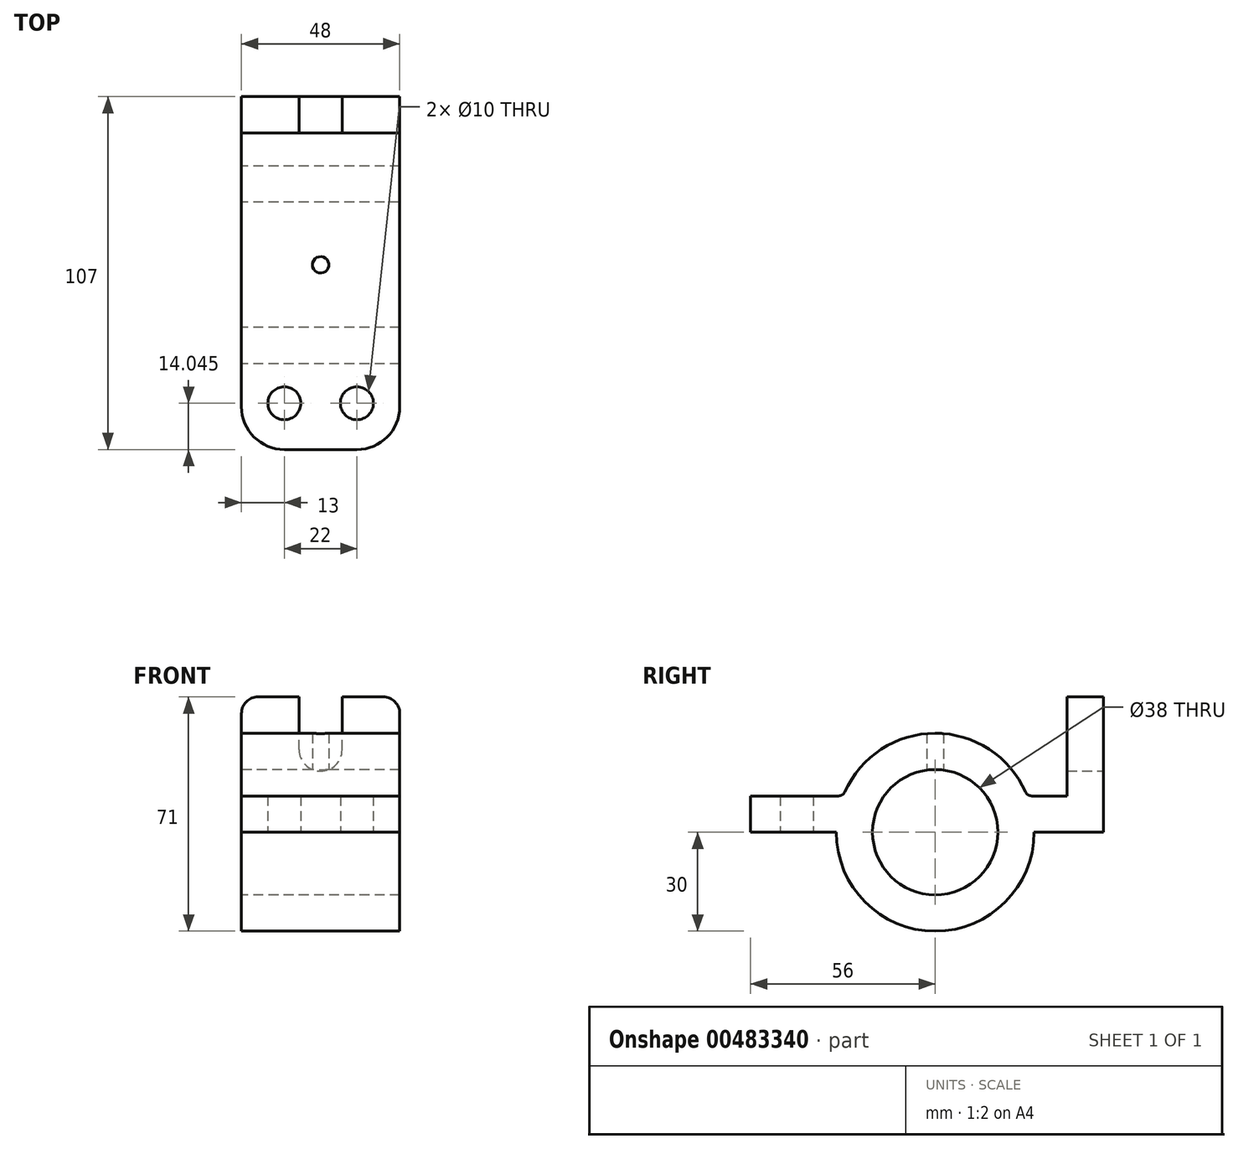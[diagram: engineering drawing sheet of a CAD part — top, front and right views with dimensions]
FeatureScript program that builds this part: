
annotation { "Feature Type Name" : "Feature", "Feature Type Description" : "" }
export const myFeature = defineFeature(function(context is Context, id is Id, definition is map)
    precondition{}
    {
        {
            var Q0;
            Q0=qCreatedBy(makeId("Right.planeOp"),FACE);
            var sketch = newSketch(context, id + "F0", { "sketchPlane" : qUnion([Q0])});
            skCircle(sketch, "E0", {"center": v(0, 0) * mm, "radius": 19 * mm});
            skCircle(sketch, "E1", {"center": v(0, 0) * mm, "radius": 30 * mm});
            skLineSegment(sketch, "E2.bottom", {"start": v(-56, 0) * mm, "end": v(51, 0) * mm});
            skLineSegment(sketch, "E2.top", {"start": v(-56, 11) * mm, "end": v(51, 11) * mm});
            skLineSegment(sketch, "E2.left", {"start": v(-56, 0) * mm, "end": v(-56, 11) * mm});
            skLineSegment(sketch, "E2.right", {"start": v(51, 0) * mm, "end": v(51, 11) * mm});
            skLineSegment(sketch, "E3.bottom", {"start": v(51, 11) * mm, "end": v(40, 11) * mm});
            skLineSegment(sketch, "E3.top", {"start": v(51, 41) * mm, "end": v(40, 41) * mm});
            skLineSegment(sketch, "E3.left", {"start": v(51, 11) * mm, "end": v(51, 41) * mm});
            skLineSegment(sketch, "E3.right", {"start": v(40, 11) * mm, "end": v(40, 41) * mm});
            skSolve(sketch);
        }
        {
            var Q0;
            Q0 = qSketchRegion(id + "F2", true);
            var Q1;
            Q1 = qSketchRegion(id + "F0", true);
            extrude(context, id + "F1", {"entities" : qUnion([Q0, Q1]), "depth" : 48 * mm, "symmetric" : true});
        }
        {
            var Q0;
            Q0=makeQuery(id+"F1.opExtrude","SWEPT_FACE",FACE,{"disambiguationData":[OSD([sQuery(id+"F0.wireOp",EDGE,"E2.right"),sQuery(id+"F0.wireOp",EDGE,"E3.left")])]});
            var sketch = newSketch(context, id + "F2", { "sketchPlane" : qUnion([Q0])});
            skLineSegment(sketch, "E4", {"start": v(0, 0) * mm, "end": v(0, 41) * mm, "construction": true});
            skCircle(sketch, "E5", {"center": v(0, 25) * mm, "radius": 6.5 * mm});
            skLineSegment(sketch, "E6", {"start": v(-6.5, 25) * mm, "end": v(-6.5, 41) * mm});
            skLineSegment(sketch, "E7", {"start": v(6.5, 25) * mm, "end": v(6.5, 41) * mm});
            skSolve(sketch);
        }
        {
            var Q0;
            {var subQ0=sQuery(id+"F2.wireOp",EDGE,"E5");var subQ2=makeQuery(id+"F2.imprint","INTERSECT",VERTEX,{"derivedFrom":[subQ0,sQuery(id+"F2.wireOp",EDGE,"E6")]});Q0=makeQuery(id+"F2.imprint","IMPRINT",FACE,{"disambiguationData":[TD([[makeQuery(id+"F2.imprint","IMPRINT",EDGE,{"disambiguationData":[TD([[subQ2,1.0]])],"derivedFrom":subQ0}),1.0]])]});}
            var Q1;
            {var subQ2=sQuery(id+"F2.wireOp",EDGE,"E6");Q1=makeQuery(id+"F2.imprint","IMPRINT",FACE,{"disambiguationData":[TD([[makeQuery(id+"F2.imprint","IMPRINT",EDGE,{"derivedFrom":subQ2}),-1.0]])]});}
            var Q2;
            Q2=makeQuery(id+"F1.opExtrude","SWEPT_FACE",FACE,{"disambiguationData":[OSD([sQuery(id+"F0.wireOp",EDGE,"E3.right")])]});
            extrude(context, id + "F3", {"entities" : qUnion([Q0, Q1]), "operationType" : NewBodyOperationType.REMOVE, "endBound" : BoundingType.UP_TO_SURFACE, "oppositeDirection" : true, "endBoundEntityFace" : qUnion([Q2]), "depth" : 25 * mm});
        }
        {
            var Q0;
            Q0=qCreatedBy(makeId("Top.planeOp"),FACE);
            var sketch = newSketch(context, id + "F4", { "sketchPlane" : qUnion([Q0])});
            skCircle(sketch, "E8", {"center": v(0, 0) * mm, "radius": 2.5 * mm});
            skLineSegment(sketch, "E9", {"start": v(24, -41.96) * mm, "end": v(-24, -41.96) * mm, "construction": true});
            skLineSegment(sketch, "E10", {"start": v(0, -56) * mm, "end": v(0, -27.91) * mm, "construction": true});
            skCircle(sketch, "E11", {"center": v(-11, -41.96) * mm, "radius": 5 * mm});
            skCircle(sketch, "E12", {"center": v(11, -41.96) * mm, "radius": 5 * mm});
            skSolve(sketch);
        }
        {
            var Q0;
            Q0=qSketchRegion(id+"F4",true);
            extrude(context, id + "F5", {"entities" : qUnion([Q0]), "operationType" : NewBodyOperationType.REMOVE, "endBound" : BoundingType.THROUGH_ALL, "depth" : 25 * mm});
        }
        {
            var Q0;
            Q0=makeQuery(id+"F1.opExtrude","CAP_EDGE",EDGE,{"disambiguationData":[OSD([sQuery(id+"F0.wireOp",EDGE,"E2.left")])],"isStart":false});
            var Q1;
            Q1=makeQuery(id+"F1.opExtrude","CAP_EDGE",EDGE,{"disambiguationData":[OSD([sQuery(id+"F0.wireOp",EDGE,"E2.left")])],"isStart":true});
            fillet(context, id + "F6", {"entities" : qUnion([Q0, Q1]), "radius" : 13 * mm, "tangentPropagation" : true, "allowEdgeOverflow" : false});
        }
        {
            var Q0;
            Q0=makeQuery(id+"F1.opExtrude","CAP_EDGE",EDGE,{"disambiguationData":[OSD([sQuery(id+"F0.wireOp",EDGE,"E3.top")])],"isStart":false});
            var Q1;
            Q1=makeQuery(id+"F1.opExtrude","CAP_EDGE",EDGE,{"disambiguationData":[OSD([sQuery(id+"F0.wireOp",EDGE,"E3.top")])],"isStart":true});
            fillet(context, id + "F7", {"entities" : qUnion([Q0, Q1]), "radius" : 5 * mm, "tangentPropagation" : true, "allowEdgeOverflow" : false});
        }
        {
            var Q0;
            {var subQ0=sQuery(id+"F0.wireOp",EDGE,"E1");var subQ1=sQuery(id+"F0.wireOp",EDGE,"E2.top");Q0=makeQuery(id+"F1.opExtrude","SWEPT_EDGE",EDGE,{"disambiguationData":[OSD([subQ0,subQ1]),TDD([makeQuery(id+"F0.imprint","INTERSECT",VERTEX,{"disambiguationData":[OD(1.0)],"derivedFrom":[subQ0,subQ1]})])]});}
            var Q1;
            {var subQ0=sQuery(id+"F0.wireOp",EDGE,"E1");var subQ1=sQuery(id+"F0.wireOp",EDGE,"E2.top");Q1=makeQuery(id+"F1.opExtrude","SWEPT_EDGE",EDGE,{"disambiguationData":[OSD([subQ0,subQ1]),TDD([makeQuery(id+"F0.imprint","INTERSECT",VERTEX,{"disambiguationData":[OD(0.0)],"derivedFrom":[subQ0,subQ1]})])]});}
            fillet(context, id + "F8", {"entities" : qUnion([Q0, Q1]), "radius" : 2 * mm, "tangentPropagation" : true, "allowEdgeOverflow" : false});
        }
    });
